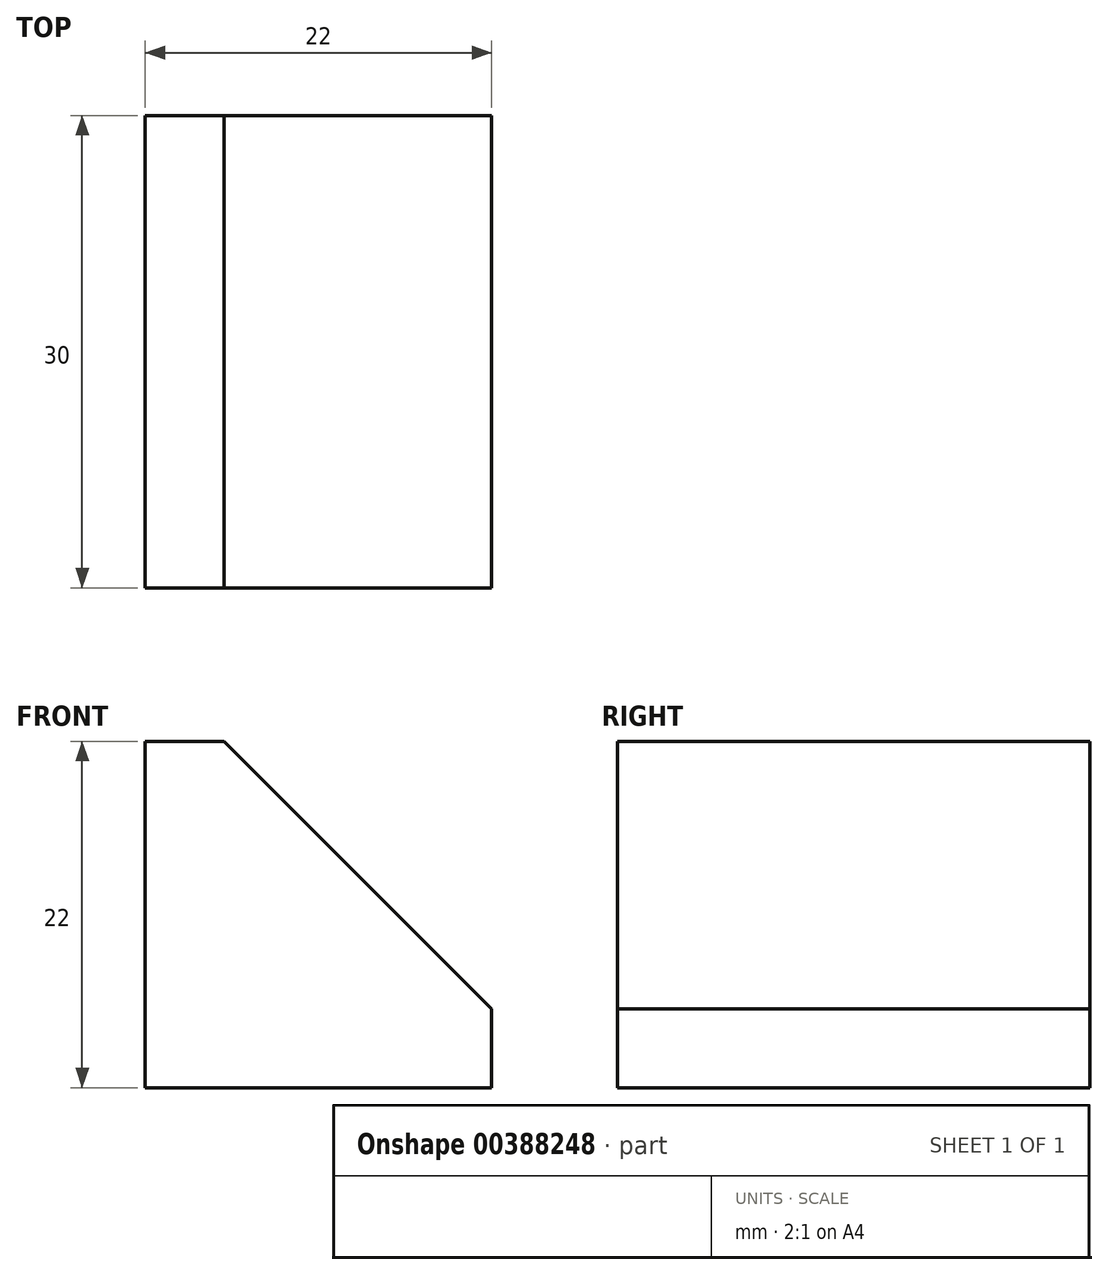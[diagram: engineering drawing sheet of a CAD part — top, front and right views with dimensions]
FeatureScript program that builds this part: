
annotation { "Feature Type Name" : "Feature", "Feature Type Description" : "" }
export const myFeature = defineFeature(function(context is Context, id is Id, definition is map)
    precondition{}
    {
        {
            var Q0;
            Q0=qCreatedBy(makeId("Front.planeOp"),FACE);
            var sketch = newSketch(context, id + "F0", { "sketchPlane" : qUnion([Q0])});
            skLineSegment(sketch, "E0", {"start": v(0, 0) * mm, "end": v(22, 0) * mm});
            skLineSegment(sketch, "E1", {"start": v(22, 0) * mm, "end": v(22, 5) * mm});
            skLineSegment(sketch, "E2", {"start": v(22, 5) * mm, "end": v(5, 22) * mm});
            skLineSegment(sketch, "E3", {"start": v(5, 22) * mm, "end": v(0, 22) * mm});
            skLineSegment(sketch, "E4", {"start": v(0, 22) * mm, "end": v(0, 0) * mm});
            skSolve(sketch);
        }
        {
            var Q0;
            Q0=makeQuery(id+"F0.imprint","IMPRINT",FACE,{"disambiguationData":[TD([[makeQuery(id+"F0.imprint","IMPRINT",EDGE,{"derivedFrom":sQuery(id+"F0.wireOp",EDGE,"E0")}),1.0]])]});
            extrude(context, id + "F1", {"entities" : qUnion([Q0]), "depth" : 30 * mm});
        }
    });
